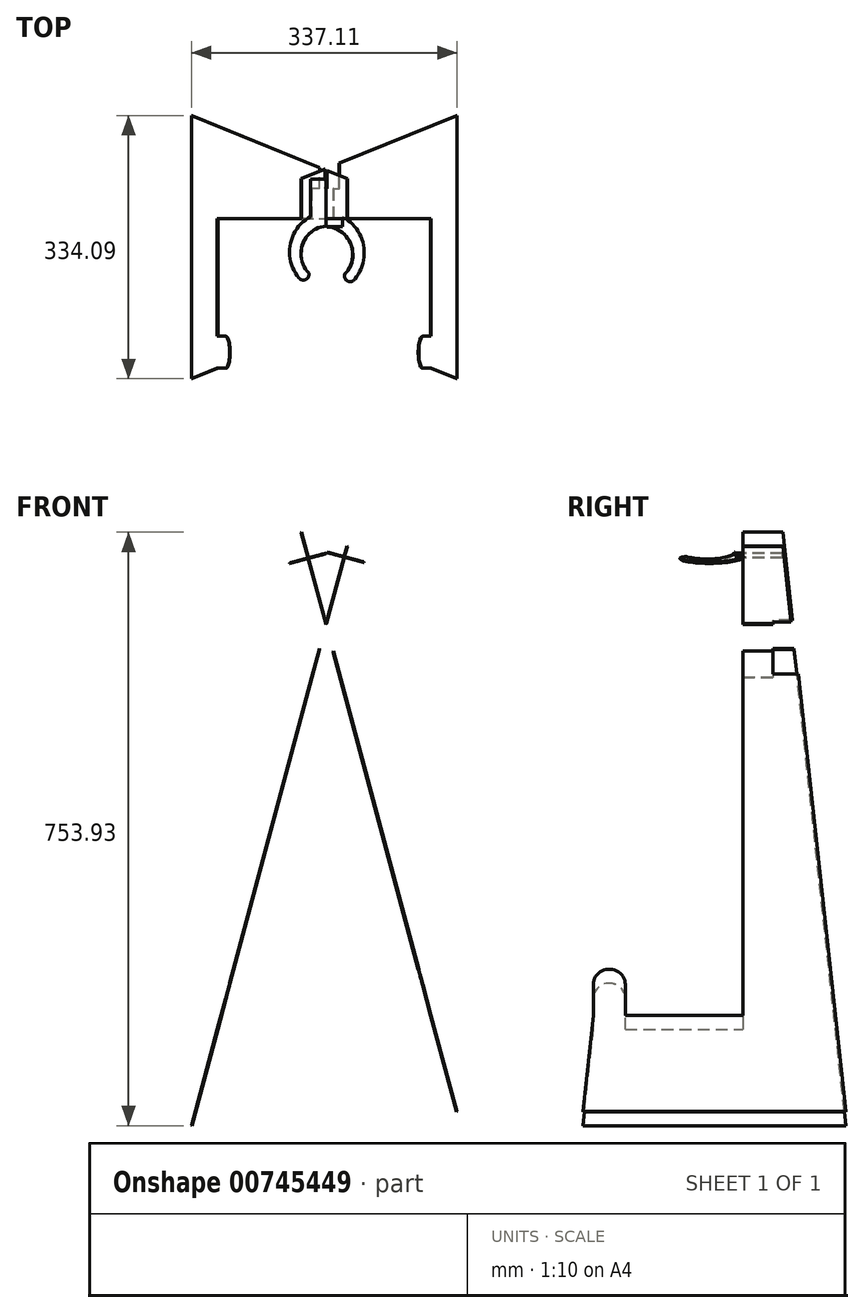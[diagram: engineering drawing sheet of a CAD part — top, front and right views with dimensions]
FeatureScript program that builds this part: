
annotation { "Feature Type Name" : "Feature", "Feature Type Description" : "" }
export const myFeature = defineFeature(function(context is Context, id is Id, definition is map)
    precondition{}
    {
        {
            assignVariable(context, id + "F0", {"name" : "ply", "anyValue" : .715});
        }
        {
            var Q0;
            Q0=qCreatedBy(makeId("Right.planeOp"),FACE);
            var sketch = newSketch(context, id + "F1", { "sketchPlane" : qUnion([Q0])});
            skLineSegment(sketch, "E0", {"start": v(0, -635.7) * mm, "end": v(0, -762) * mm});
            skLineSegment(sketch, "E1", {"start": v(0, -762) * mm, "end": v(-254, -762) * mm});
            skLineSegment(sketch, "E2", {"start": v(-254, -762) * mm, "end": v(-240.72, -635.7) * mm});
            skLineSegment(sketch, "E3", {"start": v(0, -762) * mm, "end": v(80.09, -762) * mm});
            skLineSegment(sketch, "E4", {"start": v(80.09, -762) * mm, "end": v(0, 0) * mm});
            skLineSegment(sketch, "E5", {"start": v(-240.72, -635.7) * mm, "end": v(0, -635.7) * mm});
            skLineSegment(sketch, "E6", {"start": v(0, 0) * mm, "end": v(-50.8, 0) * mm});
            skLineSegment(sketch, "E7", {"start": v(-50.8, 0) * mm, "end": v(-50.8, -635.7) * mm});
            skLineSegment(sketch, "E8", {"start": v(-50.8, -635.7) * mm, "end": v(-240.72, -635.7) * mm});
            skLineSegment(sketch, "E9", {"start": v(-240.72, -635.7) * mm, "end": v(-240.72, -762) * mm});
            skLineSegment(sketch, "E10", {"start": v(-240.72, -635.7) * mm, "end": v(-200.08, -635.7) * mm});
            skLineSegment(sketch, "E11.top", {"start": v(-240.72, -595.06) * mm, "end": v(-200.08, -595.06) * mm});
            skLineSegment(sketch, "E11.left", {"start": v(-240.72, -635.7) * mm, "end": v(-240.72, -595.06) * mm});
            skLineSegment(sketch, "E11.right", {"start": v(-200.08, -635.7) * mm, "end": v(-200.08, -595.06) * mm});
            skArc(sketch, "E12", {"start": v(-200.08, -595.06) * mm, "mid": v(-220.4, -574.74) * mm, "end": v(-240.72, -595.06) * mm});
            skSolve(sketch);
        }
        {
            var Q0;
            Q0=qCreatedBy(makeId("Top.planeOp"),FACE);
            var sketch = newSketch(context, id + "F2", { "sketchPlane" : qUnion([Q0])});
            skArc(sketch, "E13", {"start": v(33.24, 38.41) * mm, "mid": v(-15.13, 48.5) * mm, "end": v(-49.19, 12.7) * mm});
            skPoint(sketch, "E14.start.orphan", {"position": v(-2.13, 0) * mm});
            skArc(sketch, "E15", {"start": v(26.94, 25.34) * mm, "mid": v(-10.66, 33.54) * mm, "end": v(-33, 2.2) * mm});
            skLineSegment(sketch, "E16.right", {"start": v(-92.57, 12.7) * mm, "end": v(-92.57, 2.2) * mm});
            skArc(sketch, "E17", {"start": v(33.1, -38.53) * mm, "mid": v(34.55, -29.13) * mm, "end": v(25.63, -25.83) * mm});
            skArc(sketch, "E18", {"start": v(26.94, 25.34) * mm, "mid": v(35.71, 29.17) * mm, "end": v(33.24, 38.41) * mm});
            skPoint(sketch, "E16.top.end.orphan", {"position": v(-92.57, -13.36) * mm});
            skArc(sketch, "E19.MirrorCS", {"start": v(26.94, -25.34) * mm, "mid": v(-10.23, -33.7) * mm, "end": v(-32.95, -3.1) * mm});
            skPoint(sketch, "E20.MirrorCS.start.orphan", {"position": v(-92.57, 0.33) * mm});
            skLineSegment(sketch, "E21.MirrorCS", {"start": v(-92.57, -12.7) * mm, "end": v(-92.57, -3.1) * mm});
            skArc(sketch, "E22.MirrorCS", {"start": v(33.24, -38.41) * mm, "mid": v(-15.13, -48.5) * mm, "end": v(-49.19, -12.7) * mm});
            skLineSegment(sketch, "E23.bottom", {"start": v(-92.57, 2.2) * mm, "end": v(-32.95, 2.2) * mm});
            skLineSegment(sketch, "E23.top", {"start": v(-92.57, -3.1) * mm, "end": v(-32.95, -3.1) * mm});
            skPoint(sketch, "E24.orphan", {"position": v(-33, 0) * mm});
            skLineSegment(sketch, "E25.bottom", {"start": v(-92.57, 2.2) * mm, "end": v(-33.21, 2.2) * mm});
            skLineSegment(sketch, "E25.top", {"start": v(-92.57, 22.52) * mm, "end": v(-33.21, 22.52) * mm});
            skLineSegment(sketch, "E25.left", {"start": v(-92.57, 2.2) * mm, "end": v(-92.57, 22.52) * mm});
            skLineSegment(sketch, "E25.right", {"start": v(-33.21, 2.2) * mm, "end": v(-33.21, 22.52) * mm});
            skLineSegment(sketch, "E26.bottom", {"start": v(-92.57, -3.1) * mm, "end": v(-33.04, -3.1) * mm});
            skLineSegment(sketch, "E26.top", {"start": v(-92.57, -23.42) * mm, "end": v(-33.04, -23.42) * mm});
            skLineSegment(sketch, "E26.left", {"start": v(-92.57, -3.1) * mm, "end": v(-92.57, -23.42) * mm});
            skLineSegment(sketch, "E26.right", {"start": v(-33.04, -3.1) * mm, "end": v(-33.04, -23.42) * mm});
            skSolve(sketch);
        }
        {
            var Q0;
            Q0 = qSketchRegion(id + "F1", true);
            extrude(context, id + "F3", {"entities" : qUnion([Q0]), "depth" : (getVariable(context, 'ply')) * mm, "offsetDistance" : 25.4 * mm});
        }
        {
            var Q0;
            Q0=makeQuery(id+"F3.opExtrude","SWEPT_BODY",BODY,{"disambiguationData":[OSD([sQuery(id+"F1.wireOp",EDGE,"E1"),sQuery(id+"F1.wireOp",EDGE,"E2"),sQuery(id+"F1.wireOp",EDGE,"E3"),sQuery(id+"F1.wireOp",EDGE,"E4"),sQuery(id+"F1.wireOp",EDGE,"E6"),sQuery(id+"F1.wireOp",EDGE,"E7"),sQuery(id+"F1.wireOp",EDGE,"E8"),sQuery(id+"F1.wireOp",EDGE,"E11.left"),sQuery(id+"F1.wireOp",EDGE,"E11.right"),sQuery(id+"F1.wireOp",EDGE,"E12")])]});
            var Q1;
            Q1=makeQuery(id+"F3.opExtrude","CAP_EDGE",EDGE,{"disambiguationData":[OSD([sQuery(id+"F1.wireOp",EDGE,"E6")])],"isStart":false});
            transform(context, id + "F4", {"entities" : qUnion([Q0]), "transformType" : TransformType.ROTATION, "transformAxis" : qUnion([Q1]), "angle" : 90 * degree, "makeCopy" : true});
        }
        {
            var Q0;
            Q0=makeQuery(id+"F4.opPattern","COPY",BODY,{"derivedFrom":makeQuery(id+"F3.opExtrude","SWEPT_BODY",BODY,{"disambiguationData":[OSD([sQuery(id+"F1.wireOp",EDGE,"E1"),sQuery(id+"F1.wireOp",EDGE,"E2"),sQuery(id+"F1.wireOp",EDGE,"E3"),sQuery(id+"F1.wireOp",EDGE,"E4"),sQuery(id+"F1.wireOp",EDGE,"E6"),sQuery(id+"F1.wireOp",EDGE,"E7"),sQuery(id+"F1.wireOp",EDGE,"E8"),sQuery(id+"F1.wireOp",EDGE,"E11.left"),sQuery(id+"F1.wireOp",EDGE,"E11.right"),sQuery(id+"F1.wireOp",EDGE,"E12")])]}),"instanceName":"1"});
            var Q1;
            Q1=makeQuery(id+"F3.opExtrude","CAP_EDGE",EDGE,{"disambiguationData":[OSD([sQuery(id+"F1.wireOp",EDGE,"E7")])],"isStart":false});
            transform(context, id + "F5", {"entities" : qUnion([Q0]), "transformType" : TransformType.TRANSLATION_DISTANCE, "transformDirection" : qUnion([Q1]), "distance" : 101.6 * mm, "makeCopy" : false});
        }
        {
            var Q0;
            Q0=makeQuery(id+"F4.opPattern","COPY",BODY,{"derivedFrom":makeQuery(id+"F3.opExtrude","SWEPT_BODY",BODY,{"disambiguationData":[OSD([sQuery(id+"F1.wireOp",EDGE,"E1"),sQuery(id+"F1.wireOp",EDGE,"E2"),sQuery(id+"F1.wireOp",EDGE,"E3"),sQuery(id+"F1.wireOp",EDGE,"E4"),sQuery(id+"F1.wireOp",EDGE,"E6"),sQuery(id+"F1.wireOp",EDGE,"E7"),sQuery(id+"F1.wireOp",EDGE,"E8"),sQuery(id+"F1.wireOp",EDGE,"E11.left"),sQuery(id+"F1.wireOp",EDGE,"E11.right"),sQuery(id+"F1.wireOp",EDGE,"E12")])]}),"instanceName":"1"});
            var Q1;
            Q1=makeQuery(id+"F3.opExtrude","SWEPT_EDGE",EDGE,{"disambiguationData":[OSD([sQuery(id+"F1.wireOp",EDGE,"E6"),sQuery(id+"F1.wireOp",EDGE,"E7")])]});
            transform(context, id + "F6", {"entities" : qUnion([Q0]), "transformType" : TransformType.TRANSLATION_DISTANCE, "transformDirection" : qUnion([Q1]), "distance" : 120.65 * mm, "makeCopy" : false});
        }
        {
            var Q0;
            Q0=makeQuery(id+"F4.opPattern","COPY",FACE,{"derivedFrom":makeQuery(id+"F3.opExtrude","CAP_FACE",FACE,{"disambiguationData":[OSD([sQuery(id+"F1.wireOp",EDGE,"E1"),sQuery(id+"F1.wireOp",EDGE,"E2"),sQuery(id+"F1.wireOp",EDGE,"E3"),sQuery(id+"F1.wireOp",EDGE,"E4"),sQuery(id+"F1.wireOp",EDGE,"E6"),sQuery(id+"F1.wireOp",EDGE,"E7"),sQuery(id+"F1.wireOp",EDGE,"E8"),sQuery(id+"F1.wireOp",EDGE,"E11.left"),sQuery(id+"F1.wireOp",EDGE,"E11.right"),sQuery(id+"F1.wireOp",EDGE,"E12")])],"isStart":false}),"instanceName":"1"});
            var sketch = newSketch(context, id + "F7", { "sketchPlane" : qUnion([Q0])});
            skLineSegment(sketch, "E27", {"start": v(0, -50.8) * mm, "end": v(0, 10.77) * mm});
            skSolve(sketch);
        }
        {
            var Q0;
            Q0=makeQuery(id+"F4.opPattern","COPY",BODY,{"derivedFrom":makeQuery(id+"F3.opExtrude","SWEPT_BODY",BODY,{"disambiguationData":[OSD([sQuery(id+"F1.wireOp",EDGE,"E1"),sQuery(id+"F1.wireOp",EDGE,"E2"),sQuery(id+"F1.wireOp",EDGE,"E3"),sQuery(id+"F1.wireOp",EDGE,"E4"),sQuery(id+"F1.wireOp",EDGE,"E6"),sQuery(id+"F1.wireOp",EDGE,"E7"),sQuery(id+"F1.wireOp",EDGE,"E8"),sQuery(id+"F1.wireOp",EDGE,"E11.left"),sQuery(id+"F1.wireOp",EDGE,"E11.right"),sQuery(id+"F1.wireOp",EDGE,"E12")])]}),"instanceName":"1"});
            var Q1;
            Q1=sQuery(id+"F7.wireOp",EDGE,"E27");
            var Q2;
            Q2=sQuery(id+"F7.wireOp",EDGE,"E27");
            transform(context, id + "F8", {"entities" : qUnion([Q0]), "transformType" : TransformType.ROTATION, "transformAxis" : qUnion([Q2]), "angle" : 60 * degree, "makeCopy" : false});
        }
        {
            var Q0;
            Q0=makeQuery(id+"F3.opExtrude","SWEPT_FACE",FACE,{"disambiguationData":[OSD([sQuery(id+"F1.wireOp",EDGE,"E7")])]});
            var sketch = newSketch(context, id + "F9", { "sketchPlane" : qUnion([Q0])});
            skLineSegment(sketch, "E28.bottom", {"start": v(0, -101.58) * mm, "end": v(18.16, -101.58) * mm});
            skLineSegment(sketch, "E28.top", {"start": v(0, -172.7) * mm, "end": v(18.16, -172.7) * mm});
            skLineSegment(sketch, "E28.left", {"start": v(0, -101.58) * mm, "end": v(0, -172.7) * mm});
            skLineSegment(sketch, "E28.right", {"start": v(18.16, -101.58) * mm, "end": v(18.16, -172.7) * mm});
            skSolve(sketch);
        }
        {
            var Q0;
            Q0 = qSketchRegion(id + "F9", true);
            extrude(context, id + "F10", {"entities" : qUnion([Q0]), "operationType" : NewBodyOperationType.REMOVE, "oppositeDirection" : true, "depth" : 38.1 * mm, "offsetDistance" : 25.4 * mm});
        }
        {
            var Q0;
            Q0=makeQuery(id+"F3.opExtrude","SWEPT_BODY",BODY,{"disambiguationData":[OSD([sQuery(id+"F1.wireOp",EDGE,"E1"),sQuery(id+"F1.wireOp",EDGE,"E2"),sQuery(id+"F1.wireOp",EDGE,"E3"),sQuery(id+"F1.wireOp",EDGE,"E4"),sQuery(id+"F1.wireOp",EDGE,"E6"),sQuery(id+"F1.wireOp",EDGE,"E7"),sQuery(id+"F1.wireOp",EDGE,"E8"),sQuery(id+"F1.wireOp",EDGE,"E11.left"),sQuery(id+"F1.wireOp",EDGE,"E11.right"),sQuery(id+"F1.wireOp",EDGE,"E12")])]});
            var Q1;
            Q1=makeQuery(id+"F4.opPattern","COPY",BODY,{"derivedFrom":makeQuery(id+"F3.opExtrude","SWEPT_BODY",BODY,{"disambiguationData":[OSD([sQuery(id+"F1.wireOp",EDGE,"E1"),sQuery(id+"F1.wireOp",EDGE,"E2"),sQuery(id+"F1.wireOp",EDGE,"E3"),sQuery(id+"F1.wireOp",EDGE,"E4"),sQuery(id+"F1.wireOp",EDGE,"E6"),sQuery(id+"F1.wireOp",EDGE,"E7"),sQuery(id+"F1.wireOp",EDGE,"E8"),sQuery(id+"F1.wireOp",EDGE,"E11.left"),sQuery(id+"F1.wireOp",EDGE,"E11.right"),sQuery(id+"F1.wireOp",EDGE,"E12")])]}),"instanceName":"1"});
            var Q2;
            Q2=makeQuery(id+"F2k2MqeAMGPtAwj_0.opExtrude","SWEPT_BODY",BODY,{"disambiguationData":[OSD([sQuery(id+"F2.wireOp",EDGE,"E13"),sQuery(id+"F2.wireOp",EDGE,"E15"),sQuery(id+"F2.wireOp",EDGE,"E16.bottom"),sQuery(id+"F2.wireOp",EDGE,"E16.right"),sQuery(id+"F2.wireOp",EDGE,"E18"),sQuery(id+"F2.wireOp",EDGE,"E23.bottom")])]});
            var Q3;
            Q3=makeQuery(id+"F2k2MqeAMGPtAwj_0.opExtrude","SWEPT_BODY",BODY,{"disambiguationData":[OSD([sQuery(id+"F2.wireOp",EDGE,"E17"),sQuery(id+"F2.wireOp",EDGE,"E19.MirrorCS"),sQuery(id+"F2.wireOp",EDGE,"E21.MirrorCS"),sQuery(id+"F2.wireOp",EDGE,"1d7c6229-7abe-43ad-a904-806814acc5c30.MirrorCS"),sQuery(id+"F2.wireOp",EDGE,"E22.MirrorCS"),sQuery(id+"F2.wireOp",EDGE,"E23.top")])]});
            var Q4;
            Q4=makeQuery(id+"F3.opExtrude","CAP_EDGE",EDGE,{"disambiguationData":[OSD([sQuery(id+"F1.wireOp",EDGE,"E1"),sQuery(id+"F1.wireOp",EDGE,"E3")])],"isStart":false});
            transform(context, id + "F11", {"entities" : qUnion([Q0, Q1, Q2, Q3]), "transformType" : TransformType.ROTATION, "transformAxis" : qUnion([Q4]), "angle" : 15 * degree, "makeCopy" : false});
        }
        {
            var Q0;
            {var subQ1=sQuery(id+"F2.wireOp",EDGE,"E25.bottom");Q0=makeQuery(id+"F2.imprint","IMPRINT",FACE,{"disambiguationData":[TD([[makeQuery(id+"F2.imprint","IMPRINT",EDGE,{"derivedFrom":subQ1}),1.0]])]});}
            var Q1;
            {var subQ2=sQuery(id+"F2.wireOp",EDGE,"E15");Q1=makeQuery(id+"F2.imprint","IMPRINT",FACE,{"disambiguationData":[TD([[makeQuery(id+"F2.imprint","IMPRINT",EDGE,{"derivedFrom":subQ2}),-1.0]])]});}
            extrude(context, id + "F12", {"entities" : qUnion([Q0, Q1]), "depth" : (getVariable(context, 'ply')) * mm, "offsetDistance" : 25.4 * mm});
        }
        {
            var Q0;
            {var subQ1=sQuery(id+"F2.wireOp",EDGE,"E26.bottom");Q0=makeQuery(id+"F2.imprint","IMPRINT",FACE,{"disambiguationData":[TD([[makeQuery(id+"F2.imprint","IMPRINT",EDGE,{"derivedFrom":subQ1}),-1.0]])]});}
            var Q1;
            {var subQ6=sQuery(id+"F2.wireOp",EDGE,"E23.top");Q1=makeQuery(id+"F2.imprint","IMPRINT",FACE,{"disambiguationData":[TD([[makeQuery(id+"F2.imprint","IMPRINT",EDGE,{"derivedFrom":subQ6}),-1.0]])]});}
            extrude(context, id + "F13", {"entities" : qUnion([Q0, Q1]), "depth" : (getVariable(context, 'ply')) * mm, "offsetDistance" : 25.4 * mm});
        }
        {
            var Q0;
            Q0=makeQuery(id+"F4.opPattern","COPY",FACE,{"derivedFrom":makeQuery(id+"F3.opExtrude","SWEPT_FACE",FACE,{"disambiguationData":[OSD([sQuery(id+"F1.wireOp",EDGE,"E7")])]}),"instanceName":"1"});
            var sketch = newSketch(context, id + "F14", { "sketchPlane" : qUnion([Q0])});
            skLineSegment(sketch, "E29", {"start": v(172.35, -192.58) * mm, "end": v(189.9, -187.88) * mm});
            skLineSegment(sketch, "E30", {"start": v(189.9, -187.88) * mm, "end": v(171.53, -119.35) * mm});
            skLineSegment(sketch, "E31", {"start": v(171.53, -119.35) * mm, "end": v(153.99, -124.05) * mm});
            skLineSegment(sketch, "E32", {"start": v(153.99, -124.05) * mm, "end": v(172.35, -192.58) * mm});
            skSolve(sketch);
        }
        {
            var Q0;
            Q0 = qSketchRegion(id + "F14", true);
            extrude(context, id + "F15", {"entities" : qUnion([Q0]), "operationType" : NewBodyOperationType.REMOVE, "oppositeDirection" : true, "depth" : 120.65 * mm, "offsetDistance" : 25.4 * mm, "hasSecondDirection" : true, "secondDirectionOppositeDirection" : true, "secondDirectionDepth" : 38.1 * mm});
        }
        {
            var Q0;
            Q0=makeQuery(id+"F3.opExtrude","SWEPT_BODY",BODY,{"disambiguationData":[OSD([sQuery(id+"F1.wireOp",EDGE,"E1"),sQuery(id+"F1.wireOp",EDGE,"E2"),sQuery(id+"F1.wireOp",EDGE,"E3"),sQuery(id+"F1.wireOp",EDGE,"E4"),sQuery(id+"F1.wireOp",EDGE,"E6"),sQuery(id+"F1.wireOp",EDGE,"E7"),sQuery(id+"F1.wireOp",EDGE,"E8"),sQuery(id+"F1.wireOp",EDGE,"E11.left"),sQuery(id+"F1.wireOp",EDGE,"E11.right"),sQuery(id+"F1.wireOp",EDGE,"E12")])]});
            var Q1;
            Q1=makeQuery(id+"F3.opExtrude","CAP_EDGE",EDGE,{"disambiguationData":[OSD([sQuery(id+"F1.wireOp",EDGE,"E1"),sQuery(id+"F1.wireOp",EDGE,"E3")])],"isStart":false});
            transform(context, id + "F16", {"entities" : qUnion([Q0]), "transformType" : TransformType.ROTATION, "transformAxis" : qUnion([Q1]), "angle" : 15 * degree, "oppositeDirection" : true, "makeCopy" : false});
        }
        {
            var Q0;
            Q0=makeQuery(id+"F4.opPattern","COPY",BODY,{"derivedFrom":makeQuery(id+"F3.opExtrude","SWEPT_BODY",BODY,{"disambiguationData":[OSD([sQuery(id+"F1.wireOp",EDGE,"E1"),sQuery(id+"F1.wireOp",EDGE,"E2"),sQuery(id+"F1.wireOp",EDGE,"E3"),sQuery(id+"F1.wireOp",EDGE,"E4"),sQuery(id+"F1.wireOp",EDGE,"E6"),sQuery(id+"F1.wireOp",EDGE,"E7"),sQuery(id+"F1.wireOp",EDGE,"E8"),sQuery(id+"F1.wireOp",EDGE,"E11.left"),sQuery(id+"F1.wireOp",EDGE,"E11.right"),sQuery(id+"F1.wireOp",EDGE,"E12")])]}),"instanceName":"1"});
            var Q1;
            Q1=makeQuery(id+"F4.opPattern","COPY",EDGE,{"derivedFrom":makeQuery(id+"F3.opExtrude","CAP_EDGE",EDGE,{"disambiguationData":[OSD([sQuery(id+"F1.wireOp",EDGE,"E1"),sQuery(id+"F1.wireOp",EDGE,"E3")])],"isStart":false}),"instanceName":"1"});
            transform(context, id + "F17", {"entities" : qUnion([Q0]), "transformType" : TransformType.ROTATION, "transformAxis" : qUnion([Q1]), "angle" : 15 * degree, "makeCopy" : false});
        }
        {
            var Q0;
            Q0=makeQuery(id+"F3.opExtrude","SWEPT_BODY",BODY,{"disambiguationData":[OSD([sQuery(id+"F1.wireOp",EDGE,"E1"),sQuery(id+"F1.wireOp",EDGE,"E2"),sQuery(id+"F1.wireOp",EDGE,"E3"),sQuery(id+"F1.wireOp",EDGE,"E4"),sQuery(id+"F1.wireOp",EDGE,"E6"),sQuery(id+"F1.wireOp",EDGE,"E7"),sQuery(id+"F1.wireOp",EDGE,"E8"),sQuery(id+"F1.wireOp",EDGE,"E11.left"),sQuery(id+"F1.wireOp",EDGE,"E11.right"),sQuery(id+"F1.wireOp",EDGE,"E12")])]});
            var Q1;
            Q1=makeQuery(id+"F3.opExtrude","CAP_EDGE",EDGE,{"disambiguationData":[OSD([sQuery(id+"F1.wireOp",EDGE,"E1"),sQuery(id+"F1.wireOp",EDGE,"E3")])],"isStart":false});
            transform(context, id + "F18", {"entities" : qUnion([Q0]), "transformType" : TransformType.ROTATION, "transformAxis" : qUnion([Q1]), "angle" : 15 * degree, "makeCopy" : false});
        }
        {
            var Q0;
            Q0=makeQuery(id+"F4.opPattern","COPY",BODY,{"derivedFrom":makeQuery(id+"F3.opExtrude","SWEPT_BODY",BODY,{"disambiguationData":[OSD([sQuery(id+"F1.wireOp",EDGE,"E1"),sQuery(id+"F1.wireOp",EDGE,"E2"),sQuery(id+"F1.wireOp",EDGE,"E3"),sQuery(id+"F1.wireOp",EDGE,"E4"),sQuery(id+"F1.wireOp",EDGE,"E6"),sQuery(id+"F1.wireOp",EDGE,"E7"),sQuery(id+"F1.wireOp",EDGE,"E8"),sQuery(id+"F1.wireOp",EDGE,"E11.left"),sQuery(id+"F1.wireOp",EDGE,"E11.right"),sQuery(id+"F1.wireOp",EDGE,"E12")])]}),"instanceName":"1"});
            var Q1;
            Q1=makeQuery(id+"F4.opPattern","COPY",EDGE,{"derivedFrom":makeQuery(id+"F3.opExtrude","CAP_EDGE",EDGE,{"disambiguationData":[OSD([sQuery(id+"F1.wireOp",EDGE,"E1"),sQuery(id+"F1.wireOp",EDGE,"E3")])],"isStart":false}),"instanceName":"1"});
            transform(context, id + "F19", {"entities" : qUnion([Q0]), "transformType" : TransformType.ROTATION, "transformAxis" : qUnion([Q1]), "angle" : 15 * degree, "oppositeDirection" : true, "makeCopy" : false});
        }
        {
            var Q0;
            Q0=makeQuery(id+"F12.opExtrude","SWEPT_BODY",BODY,{"disambiguationData":[OSD([sQuery(id+"F2.wireOp",EDGE,"E13"),sQuery(id+"F2.wireOp",EDGE,"E15"),sQuery(id+"F2.wireOp",EDGE,"E18"),sQuery(id+"F2.wireOp",EDGE,"E23.bottom"),sQuery(id+"F2.wireOp",EDGE,"E25.bottom"),sQuery(id+"F2.wireOp",EDGE,"E25.top"),sQuery(id+"F2.wireOp",EDGE,"E25.left")])]});
            transform(context, id + "F20", {"entities" : qUnion([Q0]), "transformType" : TransformType.TRANSLATION_3D, "dx" : 261.62 * mm, "dy" : -111.76 * mm, "dz" : 0 * mm, "makeCopy" : false});
        }
        {
            var Q0;
            Q0=makeQuery(id+"F12.opExtrude","SWEPT_BODY",BODY,{"disambiguationData":[OSD([sQuery(id+"F2.wireOp",EDGE,"E13"),sQuery(id+"F2.wireOp",EDGE,"E15"),sQuery(id+"F2.wireOp",EDGE,"E18"),sQuery(id+"F2.wireOp",EDGE,"E23.bottom"),sQuery(id+"F2.wireOp",EDGE,"E25.bottom"),sQuery(id+"F2.wireOp",EDGE,"E25.top"),sQuery(id+"F2.wireOp",EDGE,"E25.left")])]});
            var Q1;
            Q1=makeQuery(id+"F12.opExtrude","SWEPT_EDGE",EDGE,{"disambiguationData":[OSD([sQuery(id+"F2.wireOp",EDGE,"E15"),sQuery(id+"F2.wireOp",EDGE,"E23.bottom")])]});
            transform(context, id + "F21", {"entities" : qUnion([Q0]), "transformType" : TransformType.ROTATION, "transformAxis" : qUnion([Q1]), "angle" : 90 * degree, "makeCopy" : false});
        }
        {
            var Q0;
            Q0=makeQuery(id+"F12.opExtrude","SWEPT_BODY",BODY,{"disambiguationData":[OSD([sQuery(id+"F2.wireOp",EDGE,"E13"),sQuery(id+"F2.wireOp",EDGE,"E15"),sQuery(id+"F2.wireOp",EDGE,"E18"),sQuery(id+"F2.wireOp",EDGE,"E23.bottom"),sQuery(id+"F2.wireOp",EDGE,"E25.bottom"),sQuery(id+"F2.wireOp",EDGE,"E25.top"),sQuery(id+"F2.wireOp",EDGE,"E25.left")])]});
            transform(context, id + "F22", {"entities" : qUnion([Q0]), "transformType" : TransformType.TRANSLATION_3D, "dx" : -55.88 * mm, "dy" : 0 * mm, "dz" : -35.56 * mm, "makeCopy" : false});
        }
        {
            var Q0;
            Q0=makeQuery(id+"F12.opExtrude","SWEPT_BODY",BODY,{"disambiguationData":[OSD([sQuery(id+"F2.wireOp",EDGE,"E13"),sQuery(id+"F2.wireOp",EDGE,"E15"),sQuery(id+"F2.wireOp",EDGE,"E18"),sQuery(id+"F2.wireOp",EDGE,"E23.bottom"),sQuery(id+"F2.wireOp",EDGE,"E25.bottom"),sQuery(id+"F2.wireOp",EDGE,"E25.top"),sQuery(id+"F2.wireOp",EDGE,"E25.left")])]});
            var Q1;
            Q1=makeQuery(id+"F12.opExtrude","CAP_EDGE",EDGE,{"disambiguationData":[OSD([sQuery(id+"F2.wireOp",EDGE,"E23.bottom"),sQuery(id+"F2.wireOp",EDGE,"E25.bottom")])],"isStart":true});
            transform(context, id + "F23", {"entities" : qUnion([Q0]), "transformType" : TransformType.ROTATION, "transformAxis" : qUnion([Q1]), "angle" : 15 * degree, "oppositeDirection" : true, "makeCopy" : false});
        }
        {
            var Q0;
            Q0=makeQuery(id+"F12.opExtrude","SWEPT_BODY",BODY,{"disambiguationData":[OSD([sQuery(id+"F2.wireOp",EDGE,"E13"),sQuery(id+"F2.wireOp",EDGE,"E15"),sQuery(id+"F2.wireOp",EDGE,"E18"),sQuery(id+"F2.wireOp",EDGE,"E23.bottom"),sQuery(id+"F2.wireOp",EDGE,"E25.bottom"),sQuery(id+"F2.wireOp",EDGE,"E25.top"),sQuery(id+"F2.wireOp",EDGE,"E25.left")])]});
            transform(context, id + "F24", {"entities" : qUnion([Q0]), "transformType" : TransformType.TRANSLATION_3D, "dx" : -0.5 * mm, "dy" : 48.26 * mm, "dz" : 1.52 * mm, "makeCopy" : false});
        }
        {
            var Q0;
            Q0=makeQuery(id+"F13.opExtrude","SWEPT_BODY",BODY,{"disambiguationData":[OSD([sQuery(id+"F2.wireOp",EDGE,"E17"),sQuery(id+"F2.wireOp",EDGE,"E19.MirrorCS"),sQuery(id+"F2.wireOp",EDGE,"E22.MirrorCS"),sQuery(id+"F2.wireOp",EDGE,"E23.top"),sQuery(id+"F2.wireOp",EDGE,"E26.bottom"),sQuery(id+"F2.wireOp",EDGE,"E26.top"),sQuery(id+"F2.wireOp",EDGE,"E26.left")])]});
            var Q1;
            Q1=makeQuery(id+"F13.opExtrude","SWEPT_EDGE",EDGE,{"disambiguationData":[OSD([sQuery(id+"F2.wireOp",EDGE,"E26.top"),sQuery(id+"F2.wireOp",EDGE,"E26.left")])]});
            transform(context, id + "F25", {"entities" : qUnion([Q0]), "transformType" : TransformType.ROTATION, "transformAxis" : qUnion([Q1]), "angle" : 90 * degree, "makeCopy" : false});
        }
        {
            var Q0;
            Q0=makeQuery(id+"F13.opExtrude","SWEPT_BODY",BODY,{"disambiguationData":[OSD([sQuery(id+"F2.wireOp",EDGE,"E17"),sQuery(id+"F2.wireOp",EDGE,"E19.MirrorCS"),sQuery(id+"F2.wireOp",EDGE,"E22.MirrorCS"),sQuery(id+"F2.wireOp",EDGE,"E23.top"),sQuery(id+"F2.wireOp",EDGE,"E26.bottom"),sQuery(id+"F2.wireOp",EDGE,"E26.top"),sQuery(id+"F2.wireOp",EDGE,"E26.left")])]});
            var Q1;
            Q1=makeQuery(id+"F13.opExtrude","CAP_EDGE",EDGE,{"disambiguationData":[OSD([sQuery(id+"F2.wireOp",EDGE,"E26.top")])],"isStart":true});
            transform(context, id + "F26", {"entities" : qUnion([Q0]), "transformType" : TransformType.ROTATION, "transformAxis" : qUnion([Q1]), "angle" : 15 * degree, "makeCopy" : false});
        }
        {
            var Q0;
            Q0=makeQuery(id+"F13.opExtrude","SWEPT_BODY",BODY,{"disambiguationData":[OSD([sQuery(id+"F2.wireOp",EDGE,"E17"),sQuery(id+"F2.wireOp",EDGE,"E19.MirrorCS"),sQuery(id+"F2.wireOp",EDGE,"E22.MirrorCS"),sQuery(id+"F2.wireOp",EDGE,"E23.top"),sQuery(id+"F2.wireOp",EDGE,"E26.bottom"),sQuery(id+"F2.wireOp",EDGE,"E26.top"),sQuery(id+"F2.wireOp",EDGE,"E26.left")])]});
            transform(context, id + "F27", {"entities" : qUnion([Q0]), "transformType" : TransformType.TRANSLATION_3D, "dx" : 243.84 * mm, "dy" : 22.86 * mm, "dz" : -40.64 * mm, "makeCopy" : false});
        }
    });
